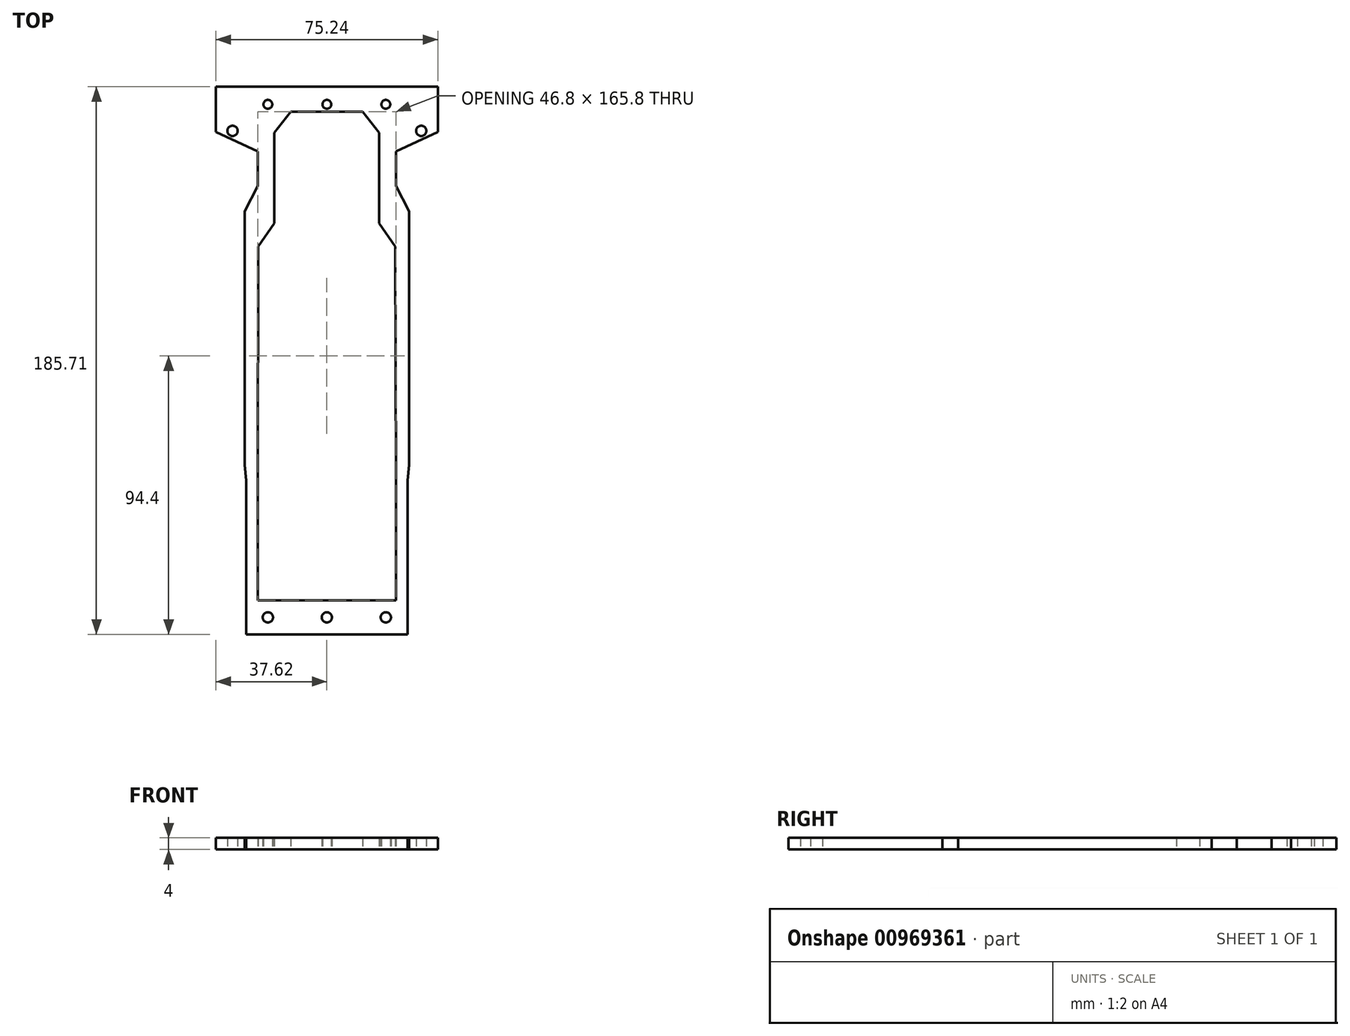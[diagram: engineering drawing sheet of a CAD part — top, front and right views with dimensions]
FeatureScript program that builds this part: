
annotation { "Feature Type Name" : "Feature", "Feature Type Description" : "" }
export const myFeature = defineFeature(function(context is Context, id is Id, definition is map)
    precondition{}
    {
        {
            var Q0;
            Q0=qCreatedBy(makeId("Top.planeOp"),FACE);
            var sketch = newSketch(context, id + "F0", { "sketchPlane" : qUnion([Q0])});
            skCircle(sketch, "E0", {"center": v(-20, 79) * mm, "radius": 1.5 * mm});
            skCircle(sketch, "E1", {"center": v(20, 79) * mm, "radius": 1.5 * mm});
            skCircle(sketch, "E2", {"center": v(0, 79) * mm, "radius": 1.5 * mm});
            skCircle(sketch, "E3", {"center": v(-32, 70) * mm, "radius": 1.75 * mm});
            skCircle(sketch, "E4", {"center": v(32, 70) * mm, "radius": 1.75 * mm});
            skCircle(sketch, "E5", {"center": v(-20, -95) * mm, "radius": 1.75 * mm});
            skCircle(sketch, "E6", {"center": v(0, -95) * mm, "radius": 1.75 * mm});
            skCircle(sketch, "E7", {"center": v(20, -95) * mm, "radius": 1.75 * mm});
            skLineSegment(sketch, "E8", {"start": v(0, 74.93) * mm, "end": v(0, 77.5) * mm});
            skLineSegment(sketch, "E9", {"start": v(0, 77.5) * mm, "end": v(0, 74.93) * mm});
            skLineSegment(sketch, "E10", {"start": v(0, 74.93) * mm, "end": v(0, 0) * mm});
            skLineSegment(sketch, "E11.MirrorCS", {"start": v(-28.3, 56.75) * mm, "end": v(-28.3, 38.21) * mm});
            skLineSegment(sketch, "E12.MirrorCS", {"start": v(-38.42, 67.47) * mm, "end": v(-28.3, 56.75) * mm});
            skLineSegment(sketch, "E13.MirrorCS", {"start": v(-28.3, 38.21) * mm, "end": v(-37.35, 27.03) * mm});
            skLineSegment(sketch, "E14.4", {"start": v(23.4, 51.3) * mm, "end": v(27.84, 42.75) * mm});
            skLineSegment(sketch, "E14.5", {"start": v(27.4, -100.75) * mm, "end": v(0, -100.75) * mm});
            skLineSegment(sketch, "E14.6", {"start": v(27.4, -61.28) * mm, "end": v(27.4, -100.75) * mm});
            skLineSegment(sketch, "E14.8", {"start": v(27.84, 42.75) * mm, "end": v(27.84, -43.24) * mm});
            skLineSegment(sketch, "E15", {"start": v(0, -89.25) * mm, "end": v(23.4, -89.25) * mm});
            skLineSegment(sketch, "E16", {"start": v(23.4, -89.25) * mm, "end": v(23.4, -61.31) * mm});
            skLineSegment(sketch, "E17", {"start": v(23.24, 30.76) * mm, "end": v(17.79, 38.7) * mm});
            skLineSegment(sketch, "E18", {"start": v(17.79, 38.7) * mm, "end": v(17.79, 57.03) * mm});
            skLineSegment(sketch, "E19", {"start": v(17.79, 57.03) * mm, "end": v(17.79, 69.4) * mm});
            skLineSegment(sketch, "E20", {"start": v(17.79, 69.4) * mm, "end": v(12.18, 76.55) * mm});
            skLineSegment(sketch, "E21", {"start": v(12.18, 76.55) * mm, "end": v(0, 76.55) * mm});
            skLineSegment(sketch, "E22", {"start": v(23.4, -61.31) * mm, "end": v(23.4, -48.1) * mm});
            skLineSegment(sketch, "E23", {"start": v(27.4, -61.28) * mm, "end": v(27.4, -48.62) * mm});
            skLineSegment(sketch, "E24", {"start": v(27.84, -43.24) * mm, "end": v(27.4, -48.62) * mm});
            skLineSegment(sketch, "E25", {"start": v(23.24, 30.76) * mm, "end": v(23.4, -48.1) * mm});
            skLineSegment(sketch, "E26", {"start": v(0, 84.96) * mm, "end": v(37.62, 84.96) * mm});
            skLineSegment(sketch, "E27", {"start": v(37.62, 84.96) * mm, "end": v(37.62, 69.6) * mm});
            skLineSegment(sketch, "E28", {"start": v(37.62, 69.6) * mm, "end": v(23.4, 63.03) * mm});
            skLineSegment(sketch, "E29", {"start": v(23.4, 63.03) * mm, "end": v(23.4, 51.3) * mm});
            skLineSegment(sketch, "E30.MirrorCS", {"start": v(0, 84.96) * mm, "end": v(-37.62, 84.96) * mm});
            skLineSegment(sketch, "E31.MirrorCS", {"start": v(-37.62, 84.96) * mm, "end": v(-37.62, 69.6) * mm});
            skLineSegment(sketch, "E32.MirrorCS", {"start": v(-37.62, 69.6) * mm, "end": v(-23.4, 63.03) * mm});
            skLineSegment(sketch, "E33.MirrorCS", {"start": v(-23.4, 63.03) * mm, "end": v(-23.4, 51.3) * mm});
            skLineSegment(sketch, "E34.MirrorCS", {"start": v(-23.4, 51.3) * mm, "end": v(-27.84, 42.75) * mm});
            skLineSegment(sketch, "E35.MirrorCS", {"start": v(-27.84, 42.75) * mm, "end": v(-27.84, -43.24) * mm});
            skLineSegment(sketch, "E36.MirrorCS", {"start": v(-27.84, -43.24) * mm, "end": v(-27.4, -48.62) * mm});
            skLineSegment(sketch, "E37.MirrorCS", {"start": v(-27.4, -61.28) * mm, "end": v(-27.4, -48.62) * mm});
            skLineSegment(sketch, "E38.MirrorCS", {"start": v(-27.4, -61.28) * mm, "end": v(-27.4, -100.75) * mm});
            skLineSegment(sketch, "E39.MirrorCS", {"start": v(-23.4, -89.25) * mm, "end": v(-23.4, -61.31) * mm});
            skLineSegment(sketch, "E40.MirrorCS", {"start": v(0, -89.25) * mm, "end": v(-23.4, -89.25) * mm});
            skLineSegment(sketch, "E41.MirrorCS", {"start": v(-23.4, -61.31) * mm, "end": v(-23.4, -48.1) * mm});
            skLineSegment(sketch, "E42.MirrorCS", {"start": v(-27.4, -100.75) * mm, "end": v(0, -100.75) * mm});
            skLineSegment(sketch, "E43.MirrorCS", {"start": v(-23.24, 30.76) * mm, "end": v(-23.4, -48.1) * mm});
            skLineSegment(sketch, "E44.MirrorCS", {"start": v(-23.24, 30.76) * mm, "end": v(-17.79, 38.7) * mm});
            skLineSegment(sketch, "E45.MirrorCS", {"start": v(-17.79, 38.7) * mm, "end": v(-17.79, 57.03) * mm});
            skLineSegment(sketch, "E46.MirrorCS", {"start": v(-17.79, 57.03) * mm, "end": v(-17.79, 69.4) * mm});
            skLineSegment(sketch, "E47.MirrorCS", {"start": v(-17.79, 69.4) * mm, "end": v(-12.18, 76.55) * mm});
            skLineSegment(sketch, "E48.MirrorCS", {"start": v(-12.18, 76.55) * mm, "end": v(0, 76.55) * mm});
            skSolve(sketch);
        }
        {
            var Q0;
            Q0=makeQuery(id+"F0.imprint","IMPRINT",FACE,{"disambiguationData":[TD([[makeQuery(id+"F0.imprint","IMPRINT",EDGE,{"derivedFrom":sQuery(id+"F0.wireOp",EDGE,"E0")}),-1.0]])]});
            extrude(context, id + "F1", {"entities" : qUnion([Q0]), "depth" : 4 * mm, "offsetDistance" : 25 * mm});
        }
    });
